# Revit family: Basin-Undercounter-American_Standard-Ovalyn-9482
name_source: partatom
category: Plumbing Fixtures
revit_build: Autodesk Revit 2014 (Build: 20130308_1515(x64)
units: mm (PartAtom-declared; Revit-internal decimal feet)

## types (1)
- 9482.000
    ADA Compliant = Yes
    Assembly Code = D2010310
    Basin Shape = Oval
    CW Connection = Yes
    CWFU = 1.5
    Cold Water Connection Diameter = 1/2"
    Cold Water Connection Height = 20 1/4"
    Cold Water Connection Radius = 1/4"
    Cold Water Connection Width = 4"
    Default Elevation = 31"
    Description = Ovalyn Universal Access undercounter sink
    HW Connection = Yes
    HWFU = 1.5
    Height = 5 1/2"
    Hot Water Connection Diameter = 1/2"
    Hot Water Connection Height = 20 1/4"
    Hot Water Connection Radius = 1/4"
    Hot Water Connection Width = 4"
    Installation Type = Undercounter
    Length = 15 3/4"
    Manufacturer = American Standard
    Material = Vitreous China-American Standard-001-White
    Model = 9482.000
    Price = Prices may vary. Please consult Manufacturer Representative for most up-to-date price list.
    Product Documentation Link = http://www.americanstandard-us.com
    Product Page URL = http://www.americanstandard-us.com
    URL = http://www.americanstandard-us.com
    Vent Connection = No
    WFU = 2
    Waste Connection = Yes
    Waste Connection Diameter = 1 1/4"
    Waste Connection Height = 18 1/8"
    Waste Connection Radius = 5/8"
    Width = 19 1/4"

## geometry (parser evidence)
native form markers: Sweep x1
no freeform markers — native parametric forms only
